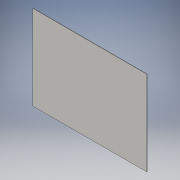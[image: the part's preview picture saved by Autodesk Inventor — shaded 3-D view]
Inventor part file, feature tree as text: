
AUTODESK INVENTOR PART (.ipt)
format: ipt  version: 2016 (Build 200138000, 138)  size: 84,992 bytes
history: native  units: in
note: dims shown in document units (in); Inventor stores cm internally (conversion verified against a paired STEP export)
features: extrude x1, sketch x1
ambient origin geometry x8: Origin, YZ Plane, XZ Plane, XY Plane, X Axis, Y Axis, Z Axis, Center Point
bodies: Solid1 (feature_tree)
feature tree (2):
  extrude  "Extrusion1"  Depth=13.0in
  sketch  "Sketch1"  dims[d0=17.5in d1=13.0in d2=0.0625in d3=0.0in]
